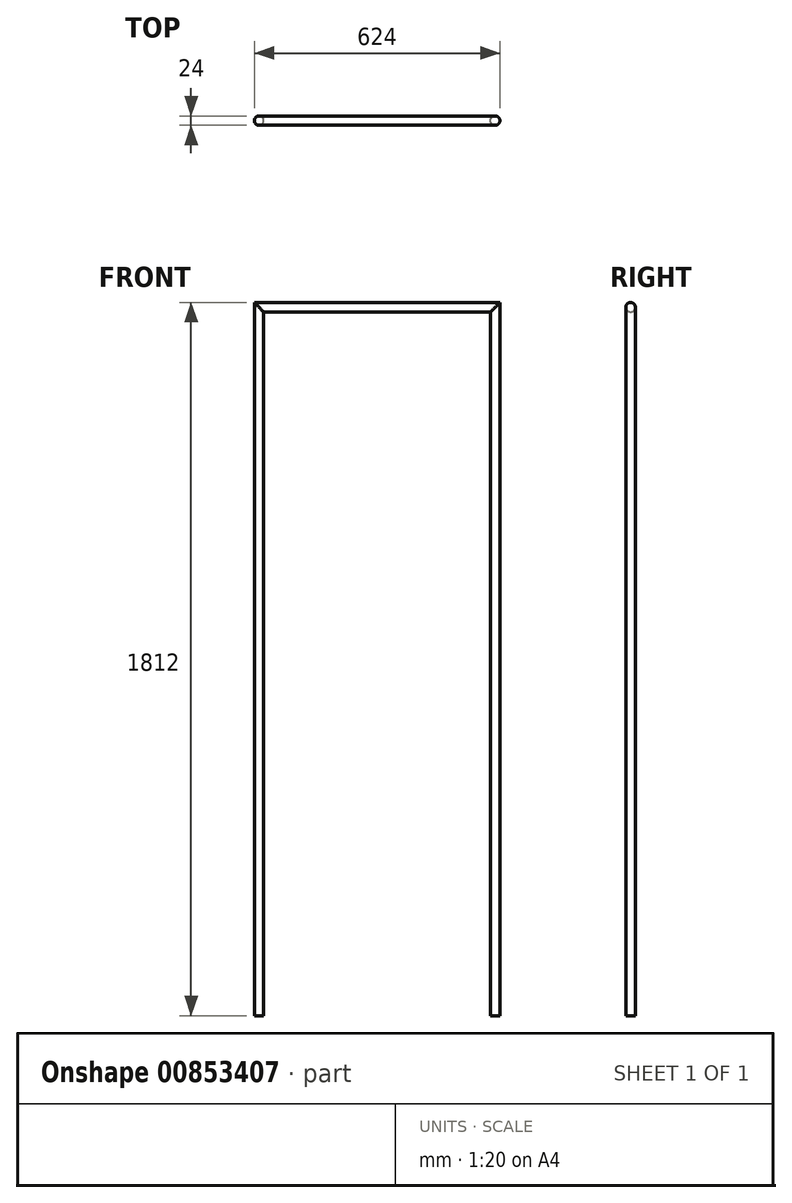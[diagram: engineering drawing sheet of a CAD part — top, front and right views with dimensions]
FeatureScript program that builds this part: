
annotation { "Feature Type Name" : "Feature", "Feature Type Description" : "" }
export const myFeature = defineFeature(function(context is Context, id is Id, definition is map)
    precondition{}
    {
        {
            var Q0;
            Q0=qCreatedBy(makeId("Front.planeOp"),FACE);
            var sketch = newSketch(context, id + "F0", { "sketchPlane" : qUnion([Q0])});
            skLineSegment(sketch, "E0", {"start": v(0, 0) * mm, "end": v(0, 1800) * mm});
            skLineSegment(sketch, "E1", {"start": v(0, 1800) * mm, "end": v(600, 1800) * mm});
            skLineSegment(sketch, "E2", {"start": v(600, 1800) * mm, "end": v(600, 0) * mm});
            skSolve(sketch);
        }
        {
            var Q0;
            Q0=qCreatedBy(makeId("Top.planeOp"),FACE);
            var sketch = newSketch(context, id + "F1", { "sketchPlane" : qUnion([Q0])});
            skCircle(sketch, "E3", {"center": v(0, 0) * mm, "radius": 12 * mm});
            skSolve(sketch);
        }
        {
            var Q0;
            Q0=makeQuery(id+"F1.imprint","IMPRINT",FACE,{"disambiguationData":[TD([[makeQuery(id+"F1.imprint","IMPRINT",EDGE,{"derivedFrom":sQuery(id+"F1.wireOp",EDGE,"E3")}),1.0]])]});
            var Q1;
            Q1=sQuery(id+"F0.wireOp",EDGE,"E0");
            var Q2;
            Q2=sQuery(id+"F0.wireOp",EDGE,"E1");
            var Q3;
            Q3=sQuery(id+"F0.wireOp",EDGE,"E2");
            sweep(context, id + "F2", {"profiles" : qUnion([Q0]), "path" : qUnion([Q1, Q2, Q3])});
        }
    });
